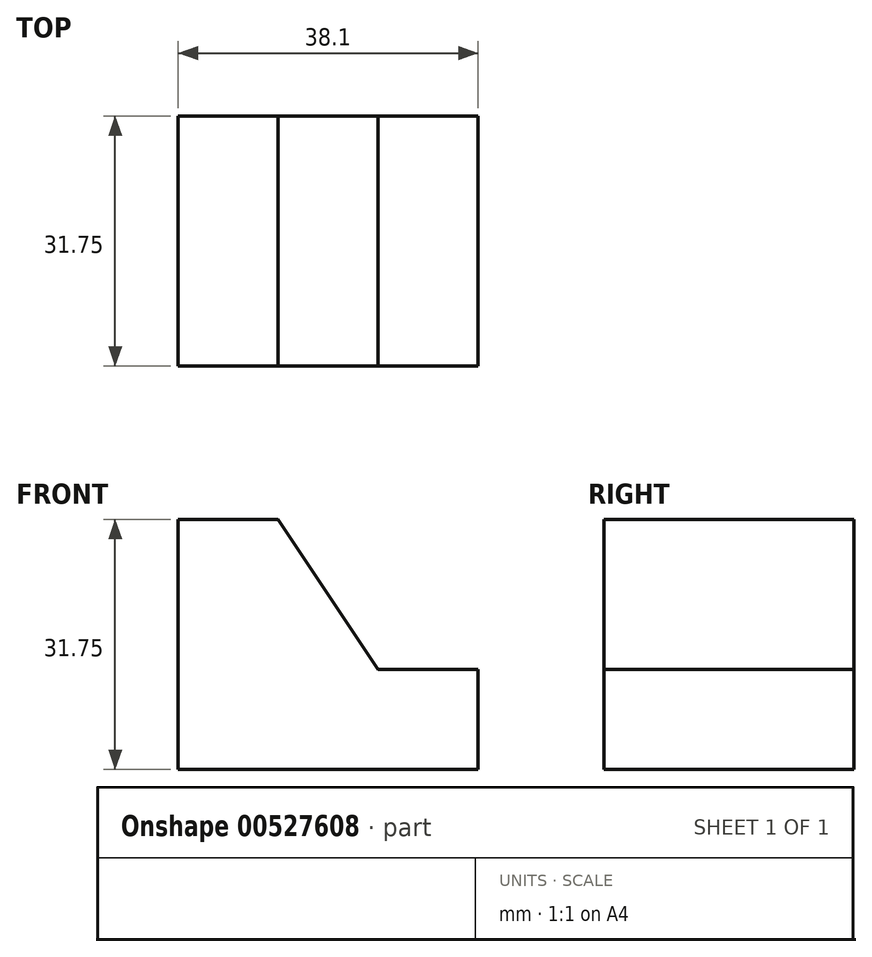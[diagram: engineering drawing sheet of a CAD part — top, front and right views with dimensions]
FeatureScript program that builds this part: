
annotation { "Feature Type Name" : "Feature", "Feature Type Description" : "" }
export const myFeature = defineFeature(function(context is Context, id is Id, definition is map)
    precondition{}
    {
        {
            var Q0;
            Q0=qCreatedBy(makeId("Front.planeOp"),FACE);
            var sketch = newSketch(context, id + "F0", { "sketchPlane" : qUnion([Q0])});
            skLineSegment(sketch, "E0", {"start": v(0, 0) * mm, "end": v(0, 31.75) * mm});
            skLineSegment(sketch, "E1", {"start": v(0, 31.75) * mm, "end": v(12.7, 31.75) * mm});
            skLineSegment(sketch, "E2", {"start": v(12.7, 31.75) * mm, "end": v(25.4, 12.7) * mm});
            skLineSegment(sketch, "E3", {"start": v(25.4, 12.7) * mm, "end": v(38.1, 12.7) * mm});
            skLineSegment(sketch, "E4", {"start": v(38.1, 12.7) * mm, "end": v(38.1, 0) * mm});
            skLineSegment(sketch, "E5", {"start": v(38.1, 0) * mm, "end": v(0, 0) * mm});
            skSolve(sketch);
        }
        {
            var Q0;
            Q0=makeQuery(id+"F0.imprint","IMPRINT",FACE,{"disambiguationData":[TD([[makeQuery(id+"F0.imprint","IMPRINT",EDGE,{"derivedFrom":sQuery(id+"F0.wireOp",EDGE,"E0")}),-1.0]])]});
            extrude(context, id + "F1", {"entities" : qUnion([Q0]), "depth" : 31.75 * mm, "offsetDistance" : 25.4 * mm});
        }
    });
